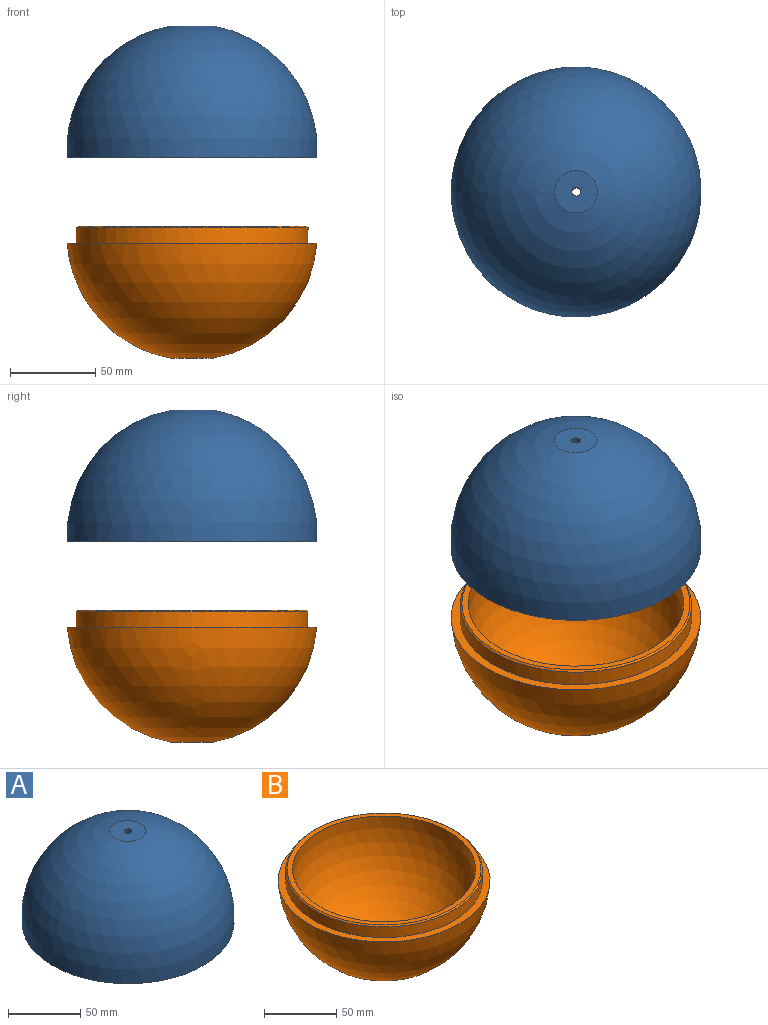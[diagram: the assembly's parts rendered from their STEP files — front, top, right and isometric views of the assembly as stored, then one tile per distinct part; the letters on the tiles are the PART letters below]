
ASSEMBLY  parts=2 mates=1
PART A: 8 faces, bbox 147x147x77.4 mm
  f0: sphere r=63.5mm, area 23320mm2, adj f5,f7
  f1: plane 25x25mm, normal (0,0,1), area 470.4mm2, adj f2,f7
  f2: sphere r=73.5mm, area 35757.9mm2, adj f1,f3
  f3: plane 146.66x146.66mm, normal (0,0,-1), area 1499.3mm2, adj f2,f6
  f4: cylinder r=69mm len=138mm, axis (0,0,-1), area 3901.9mm2, adj f5,f6
  f5: plane 138x138mm, normal (0,0,-1), area 2368mm2, adj f0,f4
  f6: cone r=69mm half-angle=45deg, axis (0,0,-1), area 617.6mm2, adj f3,f4
  f7: cylinder r=2.55mm len=8.98mm, axis (0,0,1), area 144mm2, adj f0,f1
PART B: 8 faces, bbox 146.7x146.7x77.4 mm
  f0: sphere r=63.5mm, area 27309.8mm2, adj f1,f6
  f1: plane 134x134mm, normal (0,0,1), area 1513.5mm2, adj f0,f7
  f2: cylinder r=68mm len=136mm, axis (0,0,1), area 3845.3mm2, adj f3,f7
  f3: plane 146.66x146.66mm, normal (0,0,1), area 2366.4mm2, adj f2,f4
  f4: sphere r=73.5mm, area 31139.8mm2, adj f3,f5
  f5: plane 25x25mm, normal (0,0,-1), area 470.4mm2, adj f4,f6
  f6: cylinder r=2.55mm len=8.98mm, axis (0,0,-1), area 144mm2, adj f0,f5
  f7: cone r=67mm half-angle=45deg, axis (0,0,-1), area 599.8mm2, adj f1,f2
PLACE A t=(-17.48,27.07,22.81)mm
PLACE B rot(axis=(0,0,1),180deg) t=(-17.48,27.07,-27.19)mm
MATE revolute B.f2 <-> A.f4  axis (0,0,1) through (-17.48,27.07,-27.19)mm
